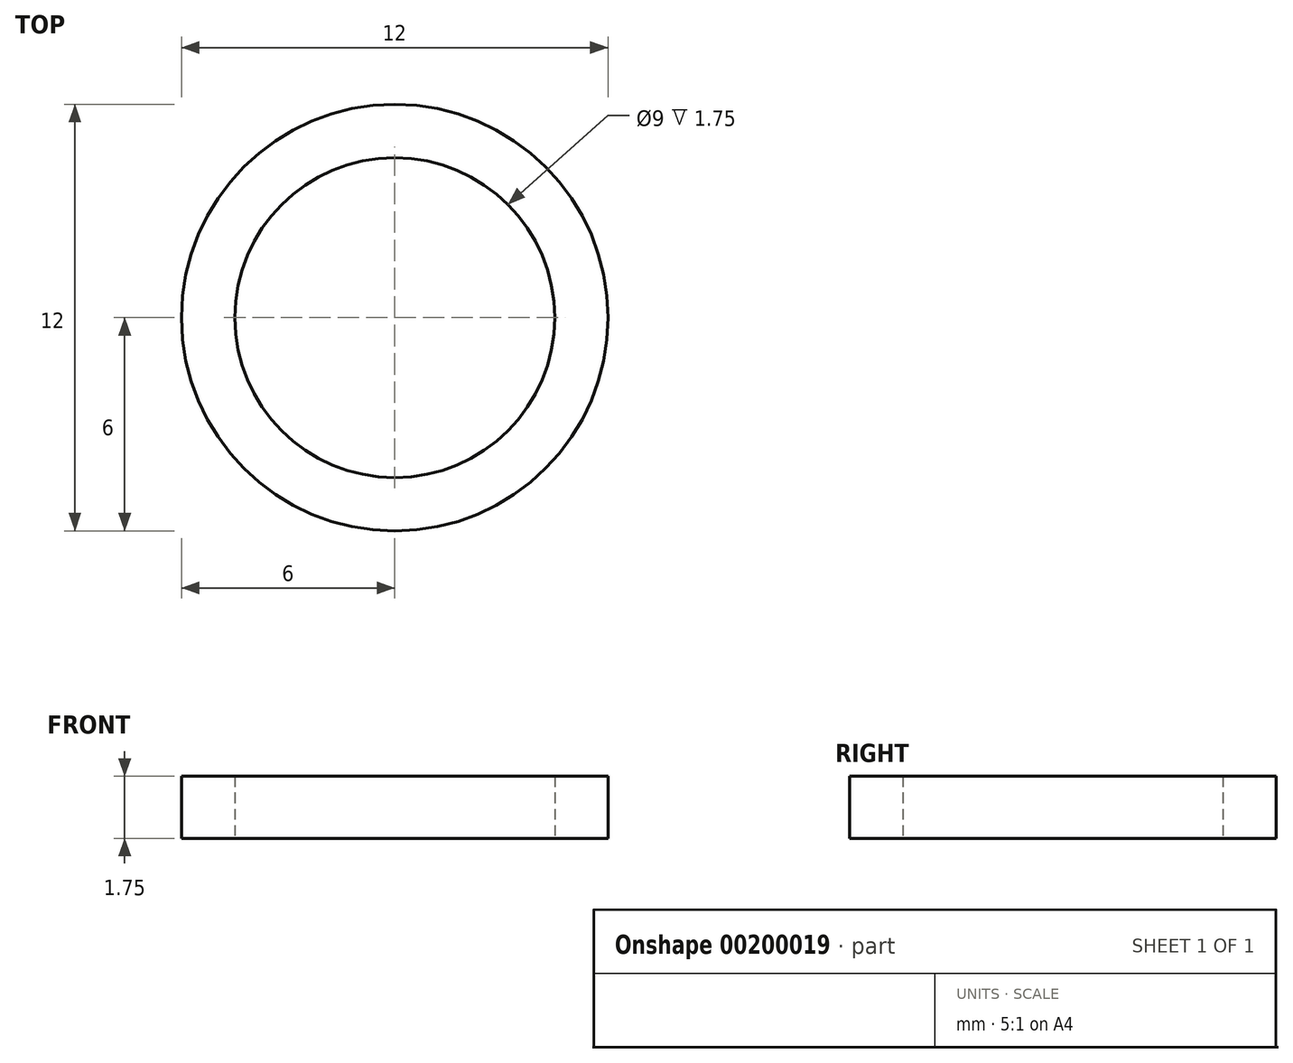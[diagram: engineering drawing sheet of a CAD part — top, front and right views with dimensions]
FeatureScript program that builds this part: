
annotation { "Feature Type Name" : "Feature", "Feature Type Description" : "" }
export const myFeature = defineFeature(function(context is Context, id is Id, definition is map)
    precondition{}
    {
        {
            var Q0;
            Q0=qCreatedBy(makeId("Top.planeOp"),FACE);
            var sketch = newSketch(context, id + "F0", { "sketchPlane" : qUnion([Q0])});
            skCircle(sketch, "E0", {"center": v(0, 0) * mm, "radius": 4.5 * mm});
            skCircle(sketch, "E1", {"center": v(0, 0) * mm, "radius": 6 * mm});
            skSolve(sketch);
        }
        {
            var Q0;
            Q0=makeQuery(id+"F0.imprint","IMPRINT",FACE,{"disambiguationData":[TD([[makeQuery(id+"F0.imprint","IMPRINT",EDGE,{"derivedFrom":sQuery(id+"F0.wireOp",EDGE,"E0")}),-1.0]])]});
            extrude(context, id + "F1", {"entities" : qUnion([Q0]), "depth" : 1.75 * mm});
        }
    });
